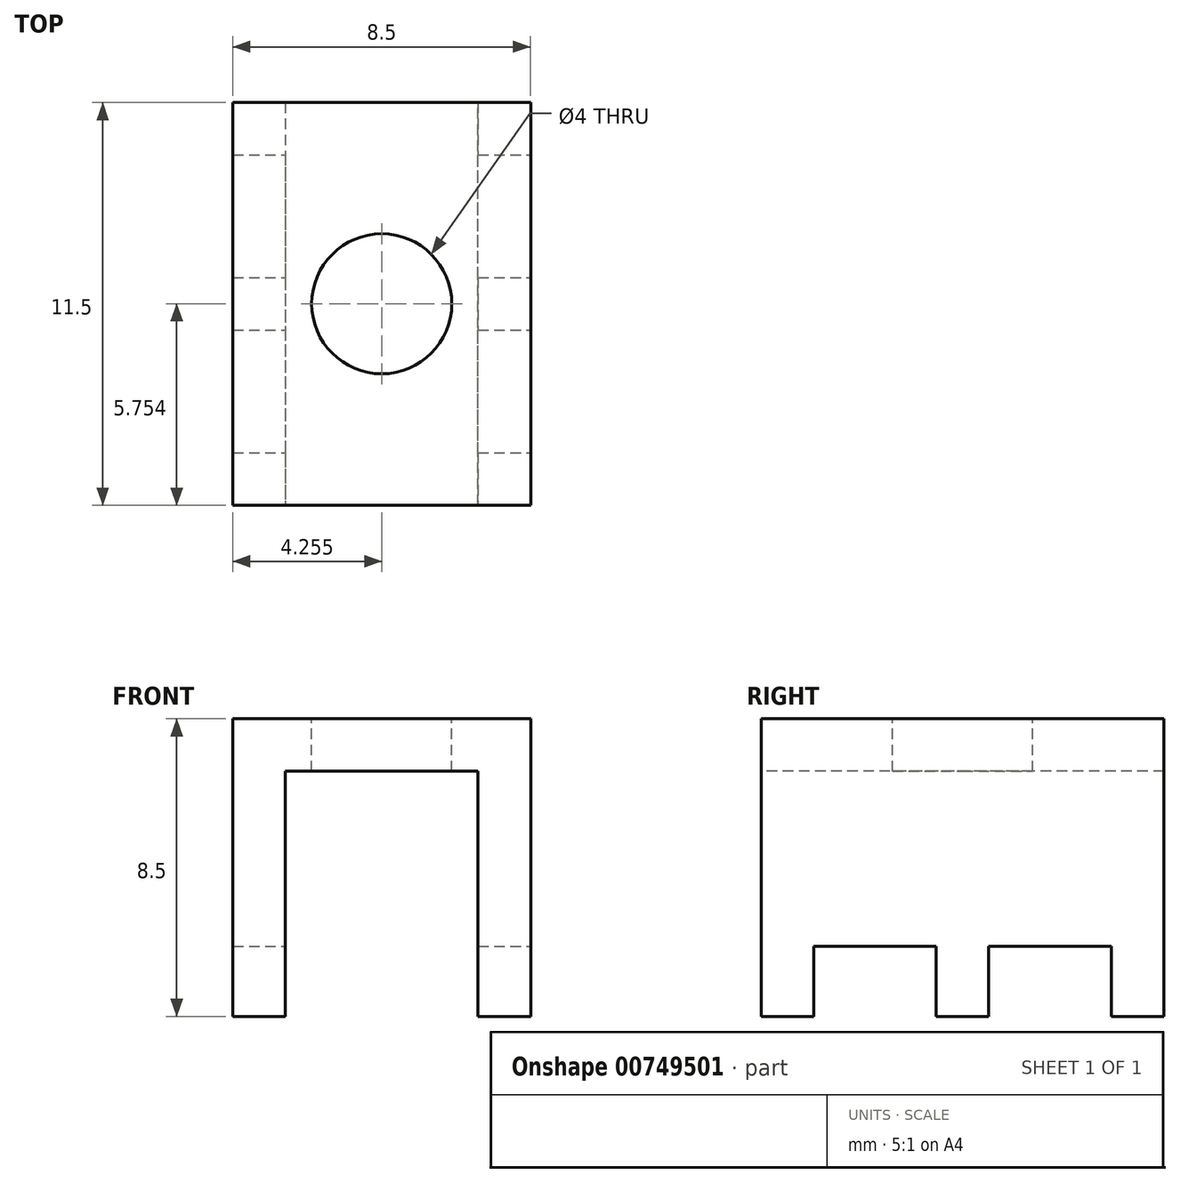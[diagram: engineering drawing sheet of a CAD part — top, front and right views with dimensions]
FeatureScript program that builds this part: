
annotation { "Feature Type Name" : "Feature", "Feature Type Description" : "" }
export const myFeature = defineFeature(function(context is Context, id is Id, definition is map)
    precondition{}
    {
        {
            var Q0;
            Q0=qCreatedBy(makeId("Top.planeOp"),FACE);
            var sketch = newSketch(context, id + "F0", { "sketchPlane" : qUnion([Q0])});
            skLineSegment(sketch, "E0.bottom", {"start": v(7.3, 8.62) * mm, "end": v(8.8, 8.62) * mm});
            skLineSegment(sketch, "E0.top", {"start": v(7.3, 7.12) * mm, "end": v(8.8, 7.12) * mm});
            skLineSegment(sketch, "E0.left", {"start": v(7.3, 8.62) * mm, "end": v(7.3, 7.12) * mm});
            skLineSegment(sketch, "E0.right", {"start": v(8.8, 8.62) * mm, "end": v(8.8, 7.12) * mm});
            skLineSegment(sketch, "E1.0.1.0", {"start": v(7.3, 12.12) * mm, "end": v(8.8, 12.12) * mm});
            skLineSegment(sketch, "E1.0.1.1", {"start": v(7.3, 13.62) * mm, "end": v(7.3, 12.12) * mm});
            skLineSegment(sketch, "E1.0.1.2", {"start": v(8.8, 13.62) * mm, "end": v(8.8, 12.12) * mm});
            skLineSegment(sketch, "E1.0.1.3", {"start": v(7.3, 13.62) * mm, "end": v(8.8, 13.62) * mm});
            skLineSegment(sketch, "E1.0.2.0", {"start": v(7.3, 17.12) * mm, "end": v(8.8, 17.12) * mm});
            skLineSegment(sketch, "E1.0.2.1", {"start": v(7.3, 18.62) * mm, "end": v(7.3, 17.12) * mm});
            skLineSegment(sketch, "E1.0.2.2", {"start": v(8.8, 18.62) * mm, "end": v(8.8, 17.12) * mm});
            skLineSegment(sketch, "E1.0.2.3", {"start": v(7.3, 18.62) * mm, "end": v(8.8, 18.62) * mm});
            skLineSegment(sketch, "E1.1.0.0", {"start": v(14.3, 7.12) * mm, "end": v(15.8, 7.12) * mm});
            skLineSegment(sketch, "E1.1.0.1", {"start": v(14.3, 8.62) * mm, "end": v(14.3, 7.12) * mm});
            skLineSegment(sketch, "E1.1.0.2", {"start": v(15.8, 8.62) * mm, "end": v(15.8, 7.12) * mm});
            skLineSegment(sketch, "E1.1.0.3", {"start": v(14.3, 8.62) * mm, "end": v(15.8, 8.62) * mm});
            skLineSegment(sketch, "E1.1.1.0", {"start": v(14.3, 12.12) * mm, "end": v(15.8, 12.12) * mm});
            skLineSegment(sketch, "E1.1.1.1", {"start": v(14.3, 13.62) * mm, "end": v(14.3, 12.12) * mm});
            skLineSegment(sketch, "E1.1.1.2", {"start": v(15.8, 13.62) * mm, "end": v(15.8, 12.12) * mm});
            skLineSegment(sketch, "E1.1.1.3", {"start": v(14.3, 13.62) * mm, "end": v(15.8, 13.62) * mm});
            skLineSegment(sketch, "E1.1.2.0", {"start": v(14.3, 17.12) * mm, "end": v(15.8, 17.12) * mm});
            skLineSegment(sketch, "E1.1.2.1", {"start": v(14.3, 18.62) * mm, "end": v(14.3, 17.12) * mm});
            skLineSegment(sketch, "E1.1.2.2", {"start": v(15.8, 18.62) * mm, "end": v(15.8, 17.12) * mm});
            skLineSegment(sketch, "E1.1.2.3", {"start": v(14.3, 18.62) * mm, "end": v(15.8, 18.62) * mm});
            skLineSegment(sketch, "E1.direction1", {"start": v(7.3, 7.12) * mm, "end": v(14.3, 7.12) * mm, "construction": true});
            skLineSegment(sketch, "E1.direction2", {"start": v(7.3, 7.12) * mm, "end": v(7.3, 12.12) * mm, "construction": true});
            skSolve(sketch);
        }
        {
            var Q0;
            Q0 = qSketchRegion(id + "F0", true);
            extrude(context, id + "F1", {"entities" : qUnion([Q0]), "depth" : 2 * mm, "offsetDistance" : 25 * mm});
        }
        {
            var Q0;
            Q0=makeQuery(id+"F1.opExtrude","CAP_FACE",FACE,{"disambiguationData":[OSD([sQuery(id+"F0.wireOp",EDGE,"E0.bottom"),sQuery(id+"F0.wireOp",EDGE,"E0.top"),sQuery(id+"F0.wireOp",EDGE,"E0.left"),sQuery(id+"F0.wireOp",EDGE,"E0.right")])],"isStart":false});
            var sketch = newSketch(context, id + "F2", { "sketchPlane" : qUnion([Q0])});
            skPoint(sketch, "E2.0", {"position": v(15.8, 18.62) * mm});
            skPoint(sketch, "E3.0", {"position": v(15.8, 7.12) * mm});
            skPoint(sketch, "E4.0", {"position": v(14.3, 18.62) * mm});
            skPoint(sketch, "E5.0", {"position": v(8.8, 18.62) * mm});
            skLineSegment(sketch, "E6.bottom", {"start": v(7.3, 7.12) * mm, "end": v(8.8, 7.12) * mm});
            skLineSegment(sketch, "E6.top", {"start": v(7.3, 18.62) * mm, "end": v(8.8, 18.62) * mm});
            skLineSegment(sketch, "E6.left", {"start": v(7.3, 7.12) * mm, "end": v(7.3, 18.62) * mm});
            skLineSegment(sketch, "E6.right", {"start": v(8.8, 7.12) * mm, "end": v(8.8, 18.62) * mm});
            skLineSegment(sketch, "E7.bottom", {"start": v(15.8, 7.12) * mm, "end": v(14.3, 7.12) * mm});
            skLineSegment(sketch, "E7.top", {"start": v(15.8, 18.62) * mm, "end": v(14.3, 18.62) * mm});
            skLineSegment(sketch, "E7.left", {"start": v(15.8, 7.12) * mm, "end": v(15.8, 18.62) * mm});
            skLineSegment(sketch, "E7.right", {"start": v(14.3, 7.12) * mm, "end": v(14.3, 18.62) * mm});
            skSolve(sketch);
        }
        {
            var Q0;
            Q0 = qSketchRegion(id + "F2", true);
            extrude(context, id + "F3", {"entities" : qUnion([Q0]), "operationType" : NewBodyOperationType.ADD, "depth" : 5 * mm, "offsetDistance" : 25 * mm});
        }
        {
            var Q0;
            Q0=makeQuery(id+"F3.opExtrude","CAP_FACE",FACE,{"disambiguationData":[OSD([sQuery(id+"F2.wireOp",EDGE,"E6.bottom"),sQuery(id+"F2.wireOp",EDGE,"E6.top"),sQuery(id+"F2.wireOp",EDGE,"E6.left"),sQuery(id+"F2.wireOp",EDGE,"E6.right")])],"isStart":false});
            var sketch = newSketch(context, id + "F4", { "sketchPlane" : qUnion([Q0])});
            skPoint(sketch, "E8.0", {"position": v(15.8, 18.62) * mm});
            skLineSegment(sketch, "E9.bottom", {"start": v(7.3, 7.12) * mm, "end": v(15.8, 7.12) * mm});
            skLineSegment(sketch, "E9.top", {"start": v(7.3, 18.62) * mm, "end": v(15.8, 18.62) * mm});
            skLineSegment(sketch, "E9.left", {"start": v(7.3, 7.12) * mm, "end": v(7.3, 18.62) * mm});
            skLineSegment(sketch, "E9.right", {"start": v(15.8, 7.12) * mm, "end": v(15.8, 18.62) * mm});
            skSolve(sketch);
        }
        {
            var Q0;
            Q0 = qSketchRegion(id + "F4", true);
            extrude(context, id + "F5", {"entities" : qUnion([Q0]), "operationType" : NewBodyOperationType.ADD, "depth" : 1.5 * mm, "offsetDistance" : 25 * mm});
        }
        {
            var Q0;
            Q0=makeQuery(id+"F5.opExtrude","CAP_FACE",FACE,{"disambiguationData":[OSD([sQuery(id+"F4.wireOp",EDGE,"E9.bottom"),sQuery(id+"F4.wireOp",EDGE,"E9.top"),sQuery(id+"F4.wireOp",EDGE,"E9.left"),sQuery(id+"F4.wireOp",EDGE,"E9.right")])],"isStart":false});
            var sketch = newSketch(context, id + "F6", { "sketchPlane" : qUnion([Q0])});
            skLineSegment(sketch, "E10", {"start": v(11.55, 18.62) * mm, "end": v(11.55, 7.12) * mm, "construction": true});
            skCircle(sketch, "E11", {"center": v(11.55, 12.87) * mm, "radius": 2 * mm});
            skSolve(sketch);
        }
        {
            var Q0;
            Q0=makeQuery(id+"F6.imprint","IMPRINT",FACE,{"disambiguationData":[TD([[makeQuery(id+"F6.imprint","IMPRINT",EDGE,{"derivedFrom":sQuery(id+"F6.wireOp",EDGE,"E11")}),1.0]])]});
            extrude(context, id + "F7", {"entities" : qUnion([Q0]), "operationType" : NewBodyOperationType.REMOVE, "oppositeDirection" : true, "depth" : 25 * mm, "offsetDistance" : 25 * mm});
        }
    });
